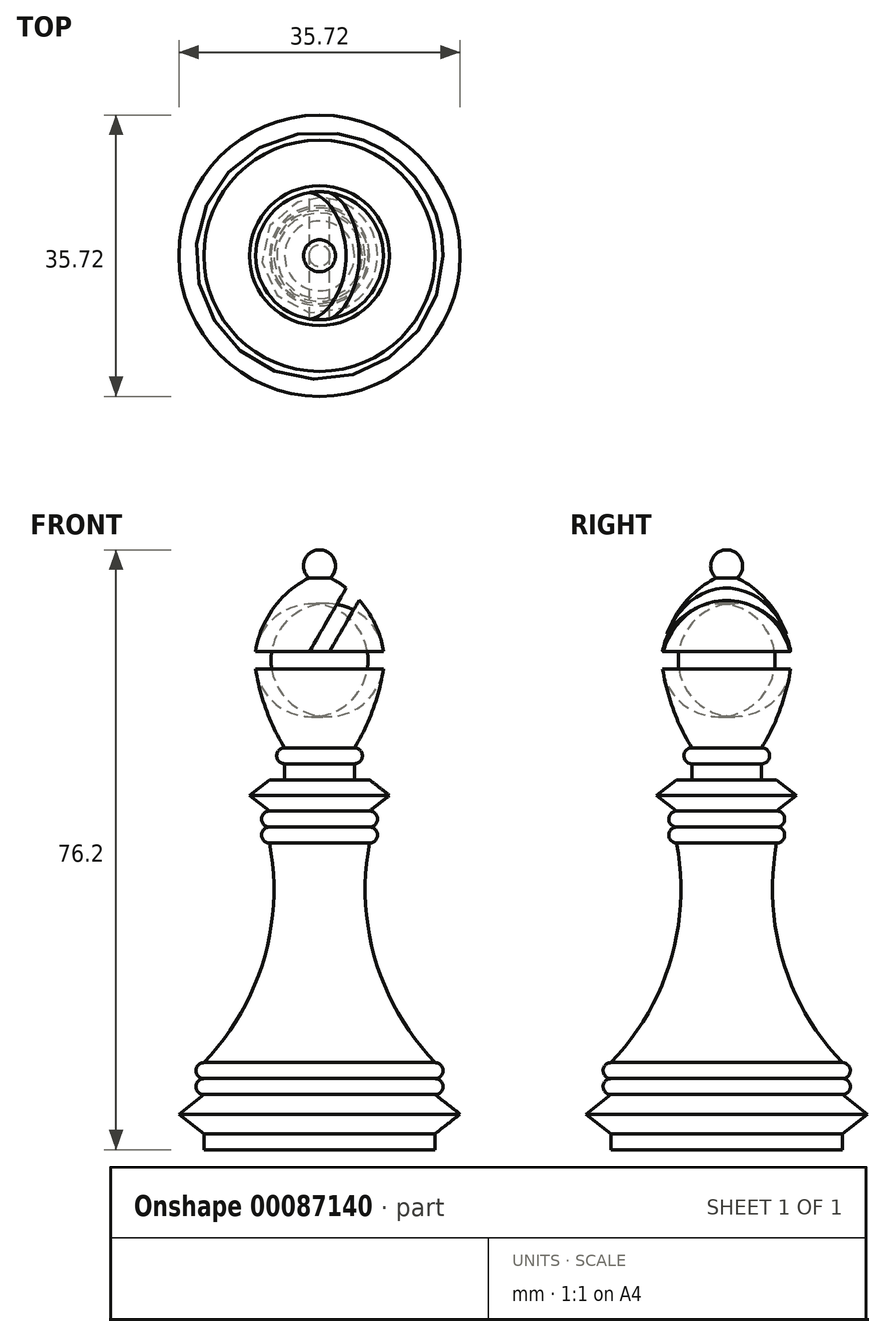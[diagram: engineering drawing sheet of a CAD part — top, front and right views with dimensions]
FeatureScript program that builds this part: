
annotation { "Feature Type Name" : "Feature", "Feature Type Description" : "" }
export const myFeature = defineFeature(function(context is Context, id is Id, definition is map)
    precondition{}
    {
        {
            var Q0;
            Q0=qCreatedBy(makeId("Front.planeOp"),FACE);
            var sketch = newSketch(context, id + "F0", { "sketchPlane" : qUnion([Q0])});
            skLineSegment(sketch, "E0", {"start": v(0, 76.2) * mm, "end": v(0, 0) * mm});
            skLineSegment(sketch, "E1", {"start": v(0, 0) * mm, "end": v(14.68, 0) * mm});
            skLineSegment(sketch, "E2", {"start": v(14.68, 0) * mm, "end": v(14.68, 2.03) * mm});
            skLineSegment(sketch, "E3", {"start": v(14.68, 2.03) * mm, "end": v(17.86, 4.51) * mm});
            skLineSegment(sketch, "E4", {"start": v(17.86, 4.51) * mm, "end": v(14.68, 7) * mm});
            skArc(sketch, "E5", {"start": v(14.68, 7) * mm, "mid": v(15.7, 8) * mm, "end": v(14.68, 9.03) * mm});
            skArc(sketch, "E6", {"start": v(14.68, 9.03) * mm, "mid": v(15.7, 10.04) * mm, "end": v(14.68, 11.06) * mm});
            skArc(sketch, "E7", {"start": v(6.35, 38.96) * mm, "mid": v(7.13, 24) * mm, "end": v(14.68, 11.06) * mm});
            skArc(sketch, "E8", {"start": v(6.35, 38.96) * mm, "mid": v(7.37, 39.97) * mm, "end": v(6.35, 40.99) * mm});
            skArc(sketch, "E9", {"start": v(6.35, 40.99) * mm, "mid": v(7.37, 42) * mm, "end": v(6.35, 43.02) * mm});
            skLineSegment(sketch, "E10", {"start": v(6.35, 43.02) * mm, "end": v(8.89, 45) * mm});
            skLineSegment(sketch, "E11", {"start": v(8.89, 45) * mm, "end": v(6.35, 47) * mm});
            skLineSegment(sketch, "E12", {"start": v(6.35, 47) * mm, "end": v(4.43, 47) * mm});
            skLineSegment(sketch, "E13", {"start": v(4.43, 46.99) * mm, "end": v(4.43, 49.02) * mm});
            skArc(sketch, "E14", {"start": v(4.43, 49.02) * mm, "mid": v(5.45, 50.04) * mm, "end": v(4.43, 51.05) * mm});
            skArc(sketch, "E15", {"start": v(1.34, 72.64) * mm, "mid": v(1.9, 74.89) * mm, "end": v(0, 76.2) * mm});
            skLineSegment(sketch, "E16", {"start": v(0, 76.2) * mm, "end": v(-4.84, 76.2) * mm, "construction": true});
            skArc(sketch, "E17", {"start": v(8.13, 63.3) * mm, "mid": v(5.86, 68.78) * mm, "end": v(1.34, 72.64) * mm});
            skArc(sketch, "E18", {"start": v(8.13, 63.3) * mm, "mid": v(8.21, 62.18) * mm, "end": v(8.13, 61.07) * mm});
            skArc(sketch, "E19", {"start": v(8.13, 61.07) * mm, "mid": v(6.78, 55.88) * mm, "end": v(4.43, 51.05) * mm});
            skLineSegment(sketch, "E20", {"start": v(14.68, 9.03) * mm, "end": v(11.62, 9.03) * mm, "construction": true});
            skLineSegment(sketch, "E21", {"start": v(14.68, 11.06) * mm, "end": v(11.64, 11.06) * mm, "construction": true});
            skLineSegment(sketch, "E22", {"start": v(6.35, 40.99) * mm, "end": v(1.05, 40.99) * mm, "construction": true});
            skLineSegment(sketch, "E23", {"start": v(6.35, 43.02) * mm, "end": v(0.76, 43.02) * mm, "construction": true});
            skLineSegment(sketch, "E24", {"start": v(4.43, 51.05) * mm, "end": v(1.11, 51.05) * mm, "construction": true});
            skSolve(sketch);
        }
        {
            var Q0;
            Q0 = qSketchRegion(id + "F0", true);
            var Q1;
            Q1=sQuery(id+"F0.wireOp",EDGE,"E0");
            revolve(context, id + "F1", {"entities" : qUnion([Q0]), "axis" : qUnion([Q1]), "revolveType" : RevolveType.FULL});
        }
        {
            var Q0;
            Q0=qCreatedBy(makeId("Front.planeOp"),FACE);
            var sketch = newSketch(context, id + "F2", { "sketchPlane" : qUnion([Q0])});
            skLineSegment(sketch, "E25", {"start": v(-1.27, 63.3) * mm, "end": v(1.27, 63.3) * mm});
            skLineSegment(sketch, "E26", {"start": v(1.27, 63.3) * mm, "end": v(6.67, 72.64) * mm});
            skLineSegment(sketch, "E27", {"start": v(6.67, 72.64) * mm, "end": v(4.13, 72.64) * mm});
            skLineSegment(sketch, "E28", {"start": v(4.13, 72.64) * mm, "end": v(-1.27, 63.3) * mm});
            skPoint(sketch, "E29", {"position": v(0, 63.3) * mm});
            skSolve(sketch);
        }
        {
            var Q0;
            Q0 = qSketchRegion(id + "F2", true);
            extrude(context, id + "F3", {"entities" : qUnion([Q0]), "operationType" : NewBodyOperationType.REMOVE, "endBound" : BoundingType.SYMMETRIC, "depth" : 25.4 * mm});
        }
    });
